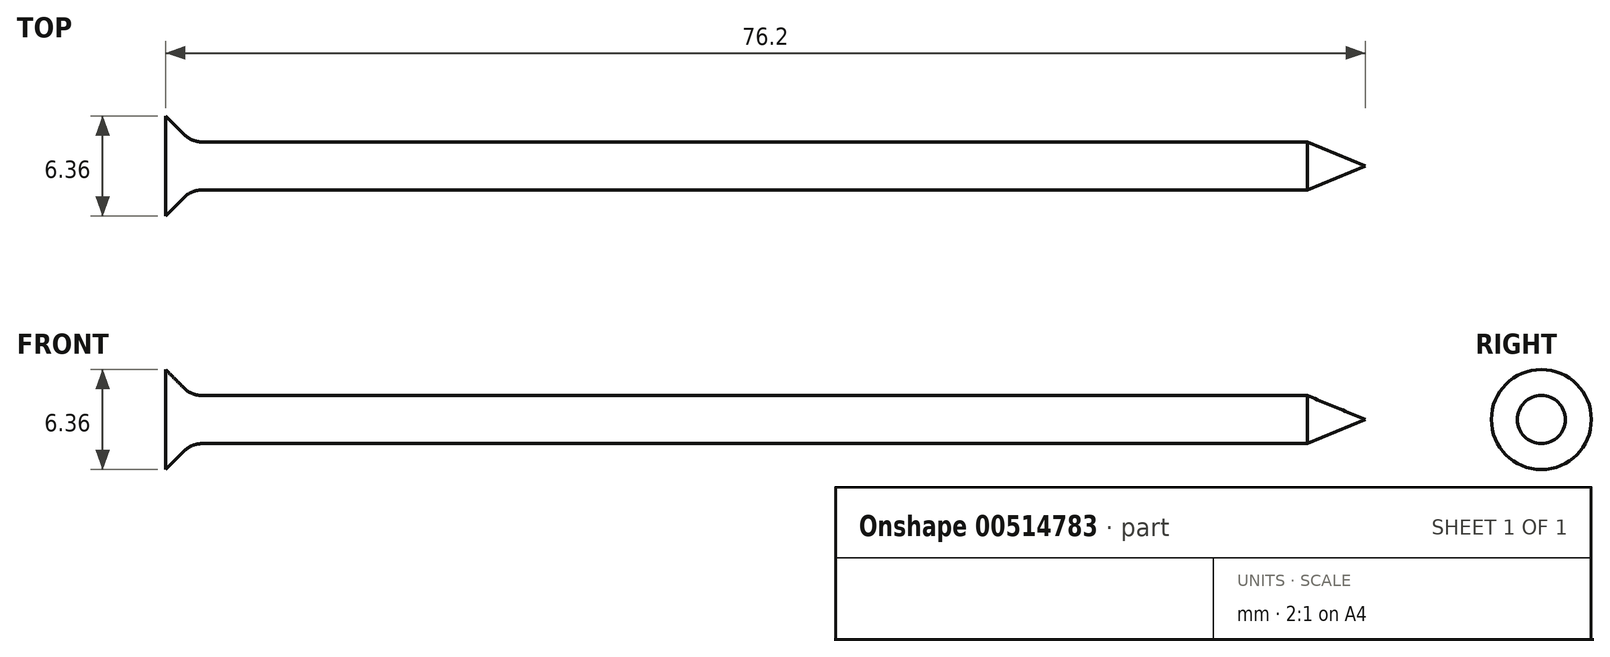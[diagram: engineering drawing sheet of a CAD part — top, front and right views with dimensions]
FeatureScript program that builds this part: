
annotation { "Feature Type Name" : "Feature", "Feature Type Description" : "" }
export const myFeature = defineFeature(function(context is Context, id is Id, definition is map)
    precondition{}
    {
        {
            var Q0;
            Q0=qCreatedBy(makeId("Front.planeOp"),FACE);
            var sketch = newSketch(context, id + "F0", { "sketchPlane" : qUnion([Q0])});
            skLineSegment(sketch, "E0", {"start": v(0, 0) * mm, "end": v(76.2, 0) * mm});
            skLineSegment(sketch, "E1", {"start": v(76.2, 0) * mm, "end": v(72.52, 1.52) * mm});
            skLineSegment(sketch, "E2", {"start": v(72.52, 1.52) * mm, "end": v(2.33, 1.52) * mm});
            skLineSegment(sketch, "E3", {"start": v(0, 0) * mm, "end": v(0, 3.17) * mm});
            skLineSegment(sketch, "E4", {"start": v(0, 3.17) * mm, "end": v(1.17, 2) * mm});
            skPoint(sketch, "E5.visualSharp", {"position": v(1.65, 1.52) * mm});
            skArc(sketch, "E5.filletArc", {"start": v(1.17, 2) * mm, "mid": v(1.7, 1.65) * mm, "end": v(2.33, 1.52) * mm});
            skSolve(sketch);
        }
        {
            var Q0;
            Q0=makeQuery(id+"F0.imprint","IMPRINT",FACE,{"disambiguationData":[TD([[makeQuery(id+"F0.imprint","IMPRINT",EDGE,{"derivedFrom":sQuery(id+"F0.wireOp",EDGE,"E0")}),1.0]])]});
            var Q1;
            Q1=sQuery(id+"F0.wireOp",EDGE,"E0");
            revolve(context, id + "F1", {"entities" : qUnion([Q0]), "axis" : qUnion([Q1]), "revolveType" : RevolveType.FULL});
        }
    });
